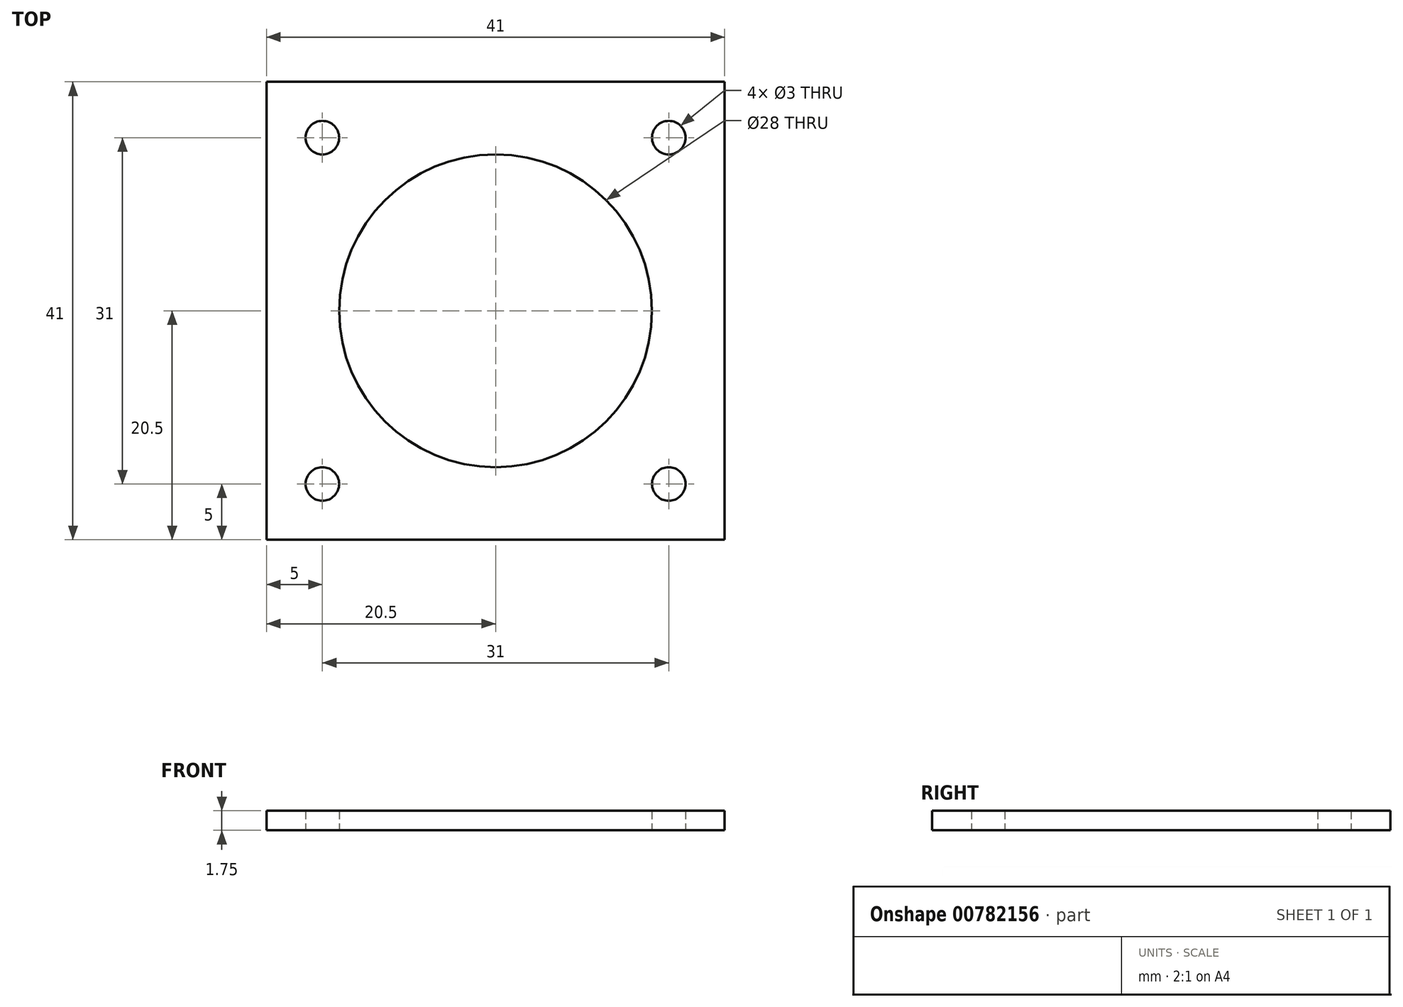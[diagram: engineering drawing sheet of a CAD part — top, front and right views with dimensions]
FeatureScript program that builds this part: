
annotation { "Feature Type Name" : "Feature", "Feature Type Description" : "" }
export const myFeature = defineFeature(function(context is Context, id is Id, definition is map)
    precondition{}
    {
        {
            var Q0;
            Q0=qCreatedBy(makeId("Top.planeOp"),FACE);
            var sketch = newSketch(context, id + "F0", { "sketchPlane" : qUnion([Q0])});
            skLineSegment(sketch, "E0.bottom", {"start": v(20.5, -20.5) * mm, "end": v(-20.5, -20.5) * mm});
            skLineSegment(sketch, "E0.top", {"start": v(20.5, 20.5) * mm, "end": v(-20.5, 20.5) * mm});
            skLineSegment(sketch, "E0.left", {"start": v(20.5, -20.5) * mm, "end": v(20.5, 20.5) * mm});
            skLineSegment(sketch, "E0.right", {"start": v(-20.5, -20.5) * mm, "end": v(-20.5, 20.5) * mm});
            skPoint(sketch, "E0.middle", {"position": v(0, 0) * mm});
            skCircle(sketch, "E1", {"center": v(-15.5, 15.5) * mm, "radius": 1.5 * mm});
            skCircle(sketch, "E2", {"center": v(15.5, 15.5) * mm, "radius": 1.5 * mm});
            skCircle(sketch, "E3", {"center": v(15.5, -15.5) * mm, "radius": 1.5 * mm});
            skCircle(sketch, "E4", {"center": v(-15.5, -15.5) * mm, "radius": 1.5 * mm});
            skLineSegment(sketch, "E5", {"start": v(-15.5, 15.5) * mm, "end": v(-15.5, -15.5) * mm});
            skLineSegment(sketch, "E6", {"start": v(15.5, -15.5) * mm, "end": v(15.5, 15.5) * mm});
            skLineSegment(sketch, "E7", {"start": v(-15.5, 15.5) * mm, "end": v(15.5, 15.5) * mm});
            skLineSegment(sketch, "E8", {"start": v(15.5, -15.5) * mm, "end": v(-15.5, -15.5) * mm});
            skLineSegment(sketch, "E9", {"start": v(-15.5, 15.5) * mm, "end": v(-15.5, 20.5) * mm});
            skLineSegment(sketch, "E10", {"start": v(15.5, 15.5) * mm, "end": v(20.5, 15.5) * mm});
            skLineSegment(sketch, "E11", {"start": v(15.5, -15.5) * mm, "end": v(15.5, -20.5) * mm});
            skLineSegment(sketch, "E12", {"start": v(-15.5, -15.5) * mm, "end": v(-20.5, -15.5) * mm});
            skCircle(sketch, "E13", {"center": v(0, 0) * mm, "radius": 14 * mm});
            skSolve(sketch);
        }
        {
            var Q0;
            Q0=makeQuery(id+"F0.imprint","IMPRINT",FACE,{"disambiguationData":[TD([[makeQuery(id+"F0.imprint","IMPRINT",EDGE,{"derivedFrom":sQuery(id+"F0.wireOp",EDGE,"E13")}),-1.0]])]});
            var Q1;
            {var subQ5=sQuery(id+"F0.wireOp",EDGE,"E0.right");var subQ6=sQuery(id+"F0.wireOp",EDGE,"E0.top");var subQ7=makeQuery(id+"F0.imprint","INTERSECT",VERTEX,{"derivedFrom":[subQ6,subQ5]});Q1=makeQuery(id+"F0.imprint","IMPRINT",FACE,{"disambiguationData":[TD([[makeQuery(id+"F0.imprint","IMPRINT",EDGE,{"disambiguationData":[TD([[subQ7,1.0]])],"derivedFrom":subQ6}),1.0]])]});}
            var Q2;
            {var subQ6=sQuery(id+"F0.wireOp",EDGE,"E0.top");var subQ11=sQuery(id+"F0.wireOp",EDGE,"E0.left");var subQ12=makeQuery(id+"F0.imprint","INTERSECT",VERTEX,{"derivedFrom":[subQ6,subQ11]});Q2=makeQuery(id+"F0.imprint","IMPRINT",FACE,{"disambiguationData":[TD([[makeQuery(id+"F0.imprint","IMPRINT",EDGE,{"disambiguationData":[TD([[subQ12,-1.0]])],"derivedFrom":subQ6}),1.0]])]});}
            var Q3;
            {var subQ9=sQuery(id+"F0.wireOp",EDGE,"E0.left");var subQ11=sQuery(id+"F0.wireOp",EDGE,"E0.bottom");var subQ12=makeQuery(id+"F0.imprint","INTERSECT",VERTEX,{"derivedFrom":[subQ11,subQ9]});Q3=makeQuery(id+"F0.imprint","IMPRINT",FACE,{"disambiguationData":[TD([[makeQuery(id+"F0.imprint","IMPRINT",EDGE,{"disambiguationData":[TD([[subQ12,-1.0]])],"derivedFrom":subQ11}),-1.0]])]});}
            var Q4;
            {var subQ9=sQuery(id+"F0.wireOp",EDGE,"E0.bottom");var subQ11=sQuery(id+"F0.wireOp",EDGE,"E0.right");var subQ12=makeQuery(id+"F0.imprint","INTERSECT",VERTEX,{"derivedFrom":[subQ9,subQ11]});Q4=makeQuery(id+"F0.imprint","IMPRINT",FACE,{"disambiguationData":[TD([[makeQuery(id+"F0.imprint","IMPRINT",EDGE,{"disambiguationData":[TD([[subQ12,1.0]])],"derivedFrom":subQ9}),-1.0]])]});}
            extrude(context, id + "F1", {"entities" : qUnion([Q0, Q1, Q2, Q3, Q4]), "depth" : 1.75 * mm, "offsetDistance" : 25 * mm});
        }
    });
